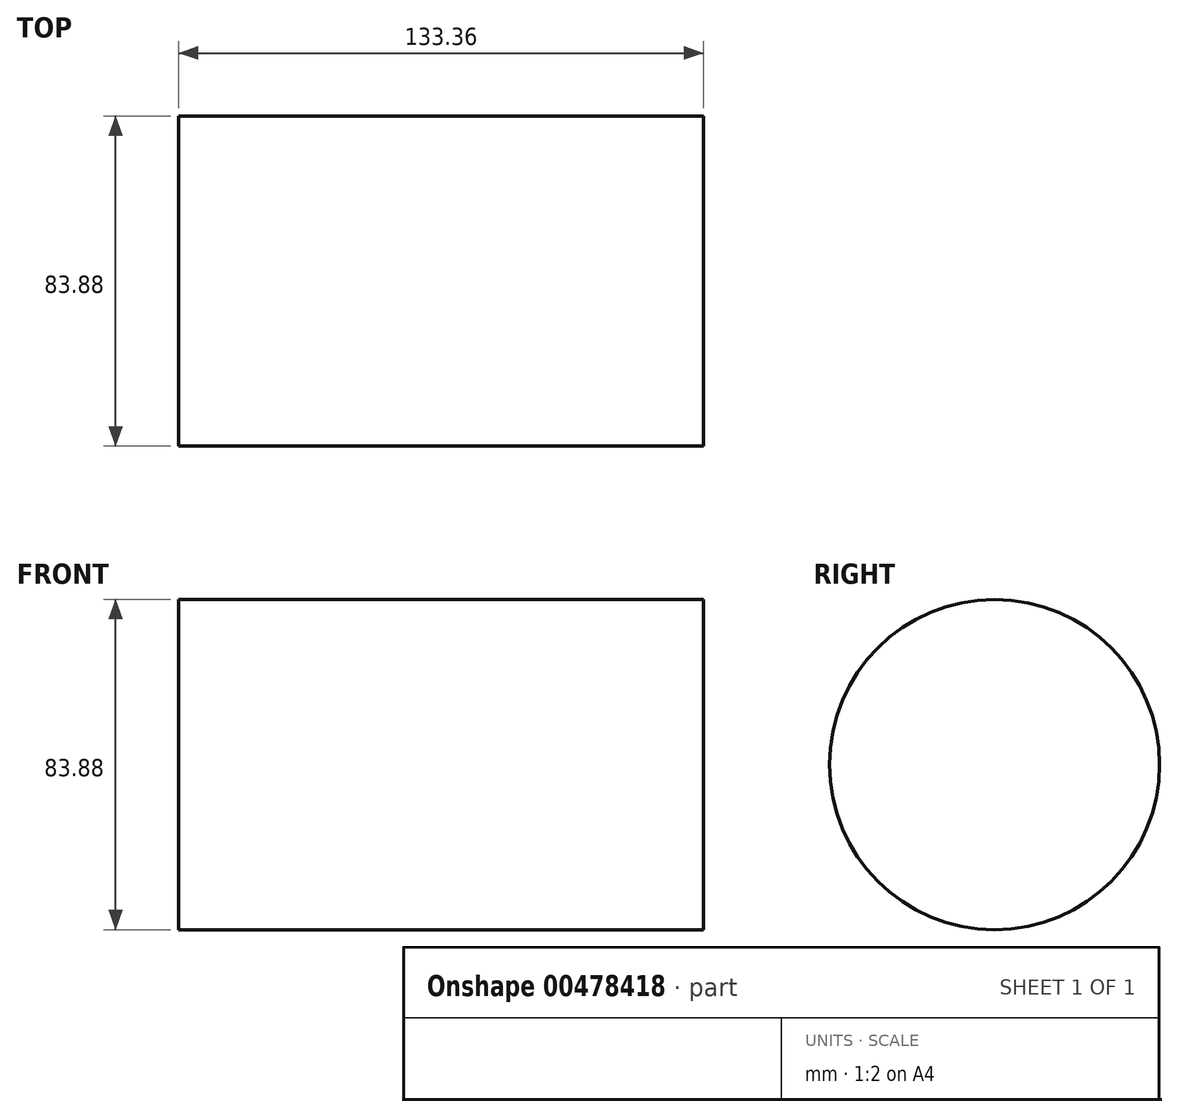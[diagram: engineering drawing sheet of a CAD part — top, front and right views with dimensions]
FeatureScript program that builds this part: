
annotation { "Feature Type Name" : "Feature", "Feature Type Description" : "" }
export const myFeature = defineFeature(function(context is Context, id is Id, definition is map)
    precondition{}
    {
        {
            var Q0;
            Q0=qCreatedBy(makeId("Right.planeOp"),FACE);
            var sketch = newSketch(context, id + "F0", { "sketchPlane" : qUnion([Q0])});
            skCircle(sketch, "E0", {"center": v(0, 0) * mm, "radius": 41.94 * mm});
            skSolve(sketch);
        }
        {
            var Q0;
            Q0=makeQuery(id+"F0.imprint","IMPRINT",FACE,{"disambiguationData":[TD([[makeQuery(id+"F0.imprint","IMPRINT",EDGE,{"derivedFrom":sQuery(id+"F0.wireOp",EDGE,"E0")}),1.0]])]});
            var Q1;
            Q1=sQuery(id+"F0.wireOp",EDGE,"E0");
            extrude(context, id + "F1", {"entities" : qUnion([Q0]), "surfaceEntities" : qUnion([Q1]), "endBound" : BoundingType.SYMMETRIC, "oppositeDirection" : true, "depth" : 133.35 * mm});
        }
    });
